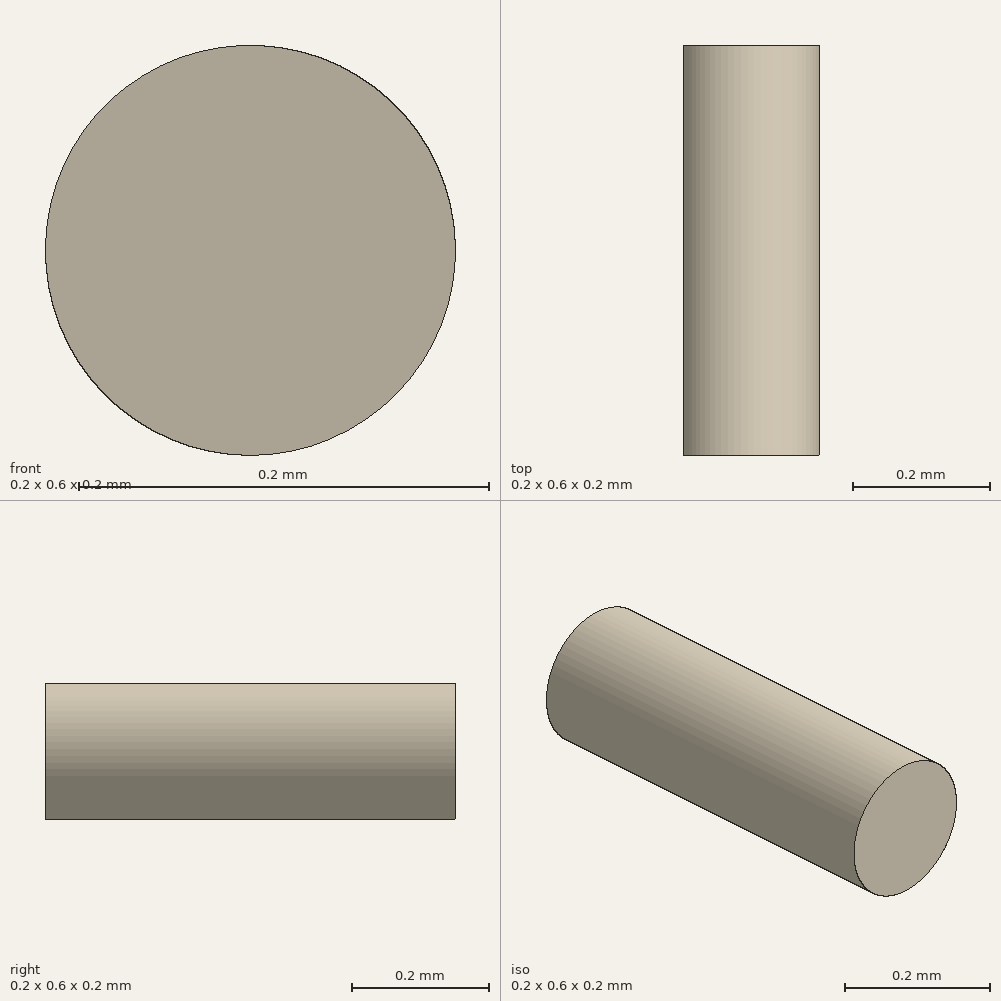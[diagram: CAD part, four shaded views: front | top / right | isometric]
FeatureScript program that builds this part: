
annotation { "Feature Type Name" : "Feature", "Feature Type Description" : "" }
export const myFeature = defineFeature(function(context is Context, id is Id, definition is map)
    precondition{}
    {
        {
            var Q0;
            Q0=qCreatedBy(makeId("Front.planeOp"),FACE);
            var sketch = newSketch(context, id + "F0", { "sketchPlane" : qUnion([Q0])});
            skCircle(sketch, "E0", {"center": v(0, 0) * mm, "radius": 0.1 * mm});
            skSolve(sketch);
        }
        {
            var Q0;
            Q0 = qSketchRegion(id + "F0", true);
            extrude(context, id + "F1", {"entities" : qUnion([Q0]), "depth" : 0.6 * mm});
        }
    });
